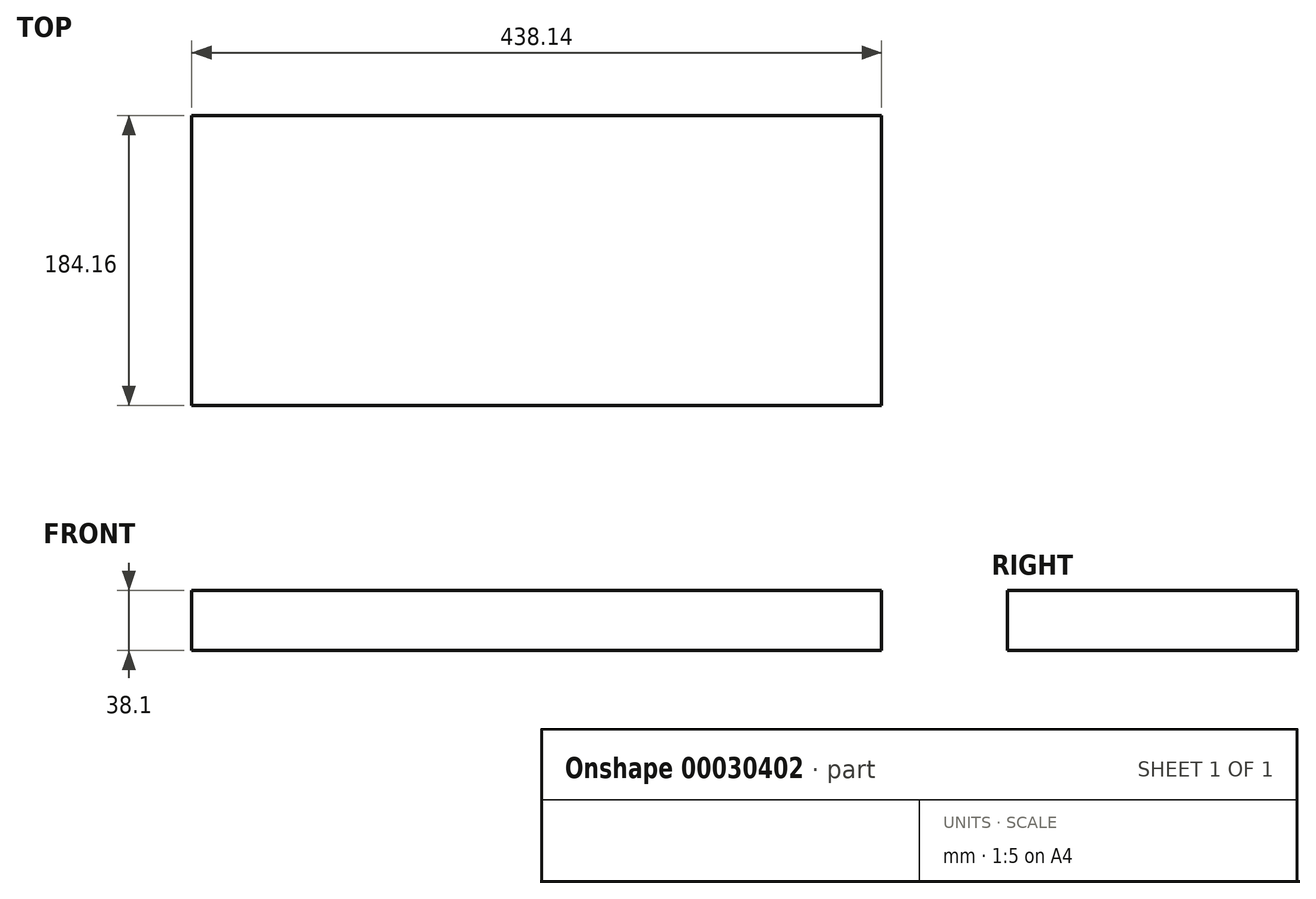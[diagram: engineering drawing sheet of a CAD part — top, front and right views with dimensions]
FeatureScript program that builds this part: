
annotation { "Feature Type Name" : "Feature", "Feature Type Description" : "" }
export const myFeature = defineFeature(function(context is Context, id is Id, definition is map)
    precondition{}
    {
        {
            var Q0;
            Q0=qCreatedBy(makeId("Top.planeOp"),FACE);
            var sketch = newSketch(context, id + "F0", { "sketchPlane" : qUnion([Q0])});
            skLineSegment(sketch, "E0.rect.bottom", {"start": v(219.08, 92.08) * mm, "end": v(-219.08, 92.08) * mm});
            skLineSegment(sketch, "E0.rect.top", {"start": v(219.08, -92.08) * mm, "end": v(-219.08, -92.08) * mm});
            skLineSegment(sketch, "E0.rect.left", {"start": v(219.08, 92.08) * mm, "end": v(219.08, -92.08) * mm});
            skLineSegment(sketch, "E0.rect.right", {"start": v(-219.08, 92.08) * mm, "end": v(-219.08, -92.08) * mm});
            skPoint(sketch, "E0.rect.middle", {"position": v(0, 0) * mm});
            skSolve(sketch);
        }
        {
            var Q0;
            Q0=makeQuery(id+"F0.imprint","IMPRINT",FACE,{"disambiguationData":[TD([[makeQuery(id+"F0.imprint","IMPRINT",EDGE,{"derivedFrom":sQuery(id+"F0.wireOp",EDGE,"E0.rect.bottom")}),1.0]])]});
            extrude(context, id + "F1", {"entities" : qUnion([Q0]), "endBound" : BoundingType.SYMMETRIC, "depth" : 38.1 * mm});
        }
    });
